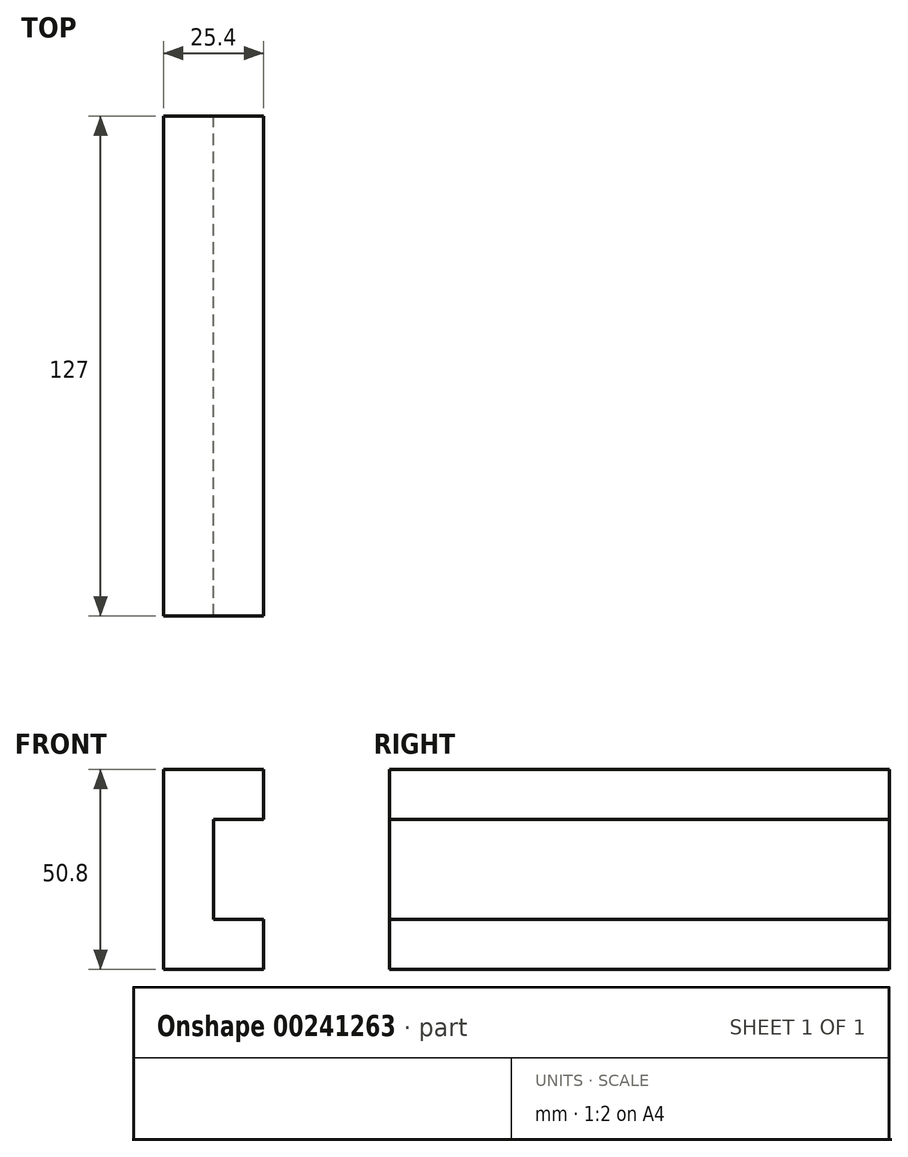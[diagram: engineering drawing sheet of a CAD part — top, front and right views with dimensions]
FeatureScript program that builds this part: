
annotation { "Feature Type Name" : "Feature", "Feature Type Description" : "" }
export const myFeature = defineFeature(function(context is Context, id is Id, definition is map)
    precondition{}
    {
        {
            var Q0;
            Q0=qCreatedBy(makeId("Front.planeOp"),FACE);
            var sketch = newSketch(context, id + "F0", { "sketchPlane" : qUnion([Q0])});
            skLineSegment(sketch, "E0", {"start": v(-63.45, 25.88) * mm, "end": v(-63.45, -24.92) * mm});
            skLineSegment(sketch, "E1", {"start": v(-63.45, -24.92) * mm, "end": v(-38.05, -24.92) * mm});
            skLineSegment(sketch, "E2", {"start": v(-38.05, -24.92) * mm, "end": v(-38.05, -12.22) * mm});
            skLineSegment(sketch, "E3", {"start": v(-38.05, -12.22) * mm, "end": v(-50.75, -12.22) * mm});
            skLineSegment(sketch, "E4", {"start": v(-63.45, 25.88) * mm, "end": v(-38.05, 25.88) * mm});
            skLineSegment(sketch, "E5", {"start": v(-38.05, 25.88) * mm, "end": v(-38.05, 13.18) * mm});
            skLineSegment(sketch, "E6", {"start": v(-38.05, 13.18) * mm, "end": v(-50.75, 13.18) * mm});
            skLineSegment(sketch, "E7", {"start": v(-50.75, 13.18) * mm, "end": v(-50.75, -12.22) * mm});
            skSolve(sketch);
        }
        {
            var Q0;
            Q0=makeQuery(id+"F0.imprint","IMPRINT",FACE,{"disambiguationData":[TD([[makeQuery(id+"F0.imprint","IMPRINT",EDGE,{"derivedFrom":sQuery(id+"F0.wireOp",EDGE,"E0")}),1.0]])]});
            extrude(context, id + "F1", {"entities" : qUnion([Q0]), "depth" : 127 * mm});
        }
    });
